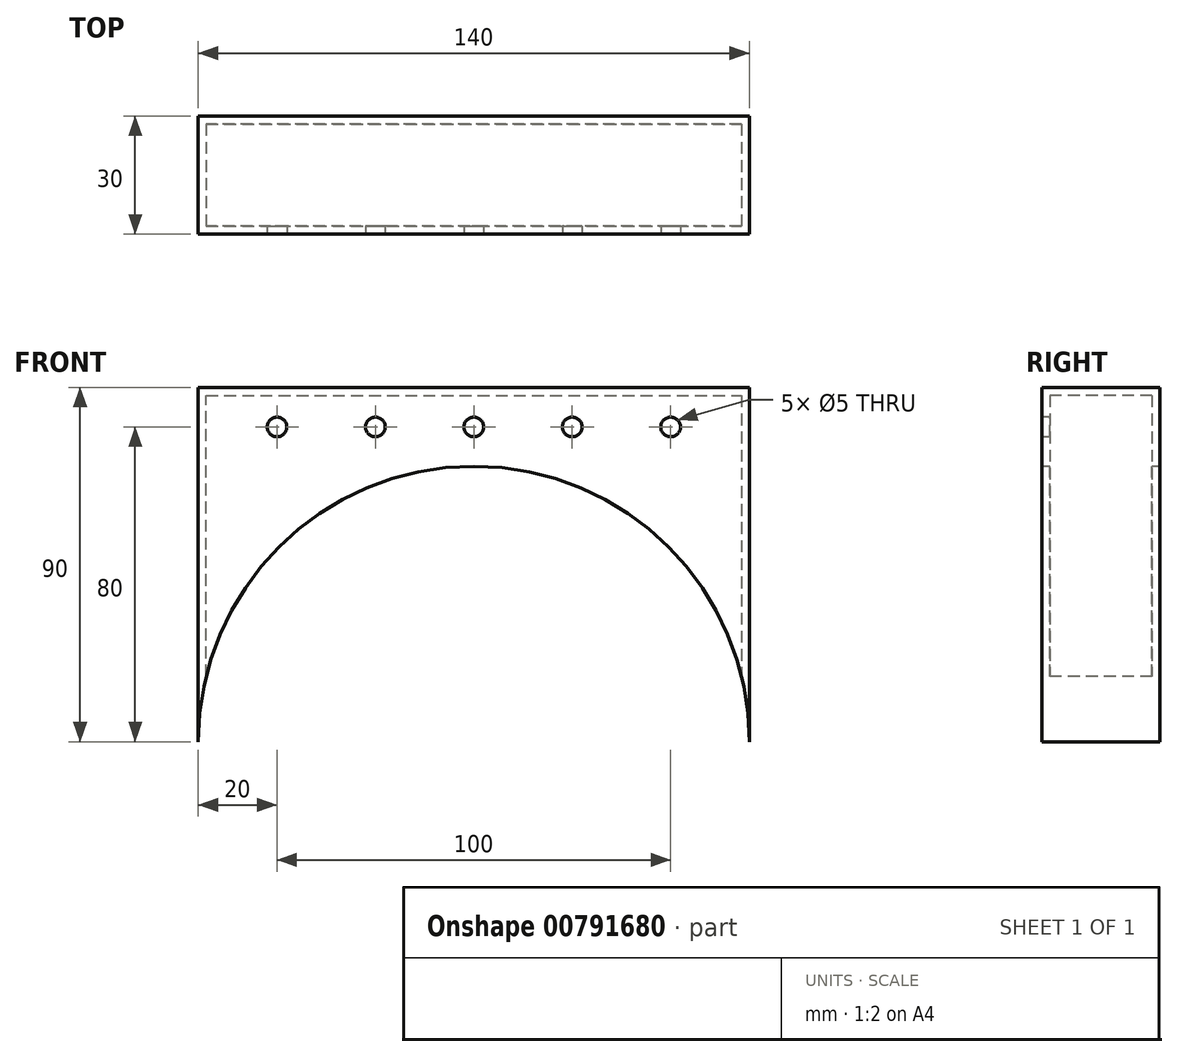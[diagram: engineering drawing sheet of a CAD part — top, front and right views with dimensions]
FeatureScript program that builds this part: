
annotation { "Feature Type Name" : "Feature", "Feature Type Description" : "" }
export const myFeature = defineFeature(function(context is Context, id is Id, definition is map)
    precondition{}
    {
        {
            var Q0;
            Q0=qCreatedBy(makeId("Front.planeOp"),FACE);
            var sketch = newSketch(context, id + "F0", { "sketchPlane" : qUnion([Q0])});
            skArc(sketch, "E0", {"start": v(70, 0) * mm, "mid": v(0, 70) * mm, "end": v(-70, 0) * mm});
            skLineSegment(sketch, "E1", {"start": v(-70, 0.4) * mm, "end": v(-70, 0) * mm});
            skLineSegment(sketch, "E2", {"start": v(-70, 0) * mm, "end": v(-70, 90) * mm});
            skLineSegment(sketch, "E3", {"start": v(-70, 90) * mm, "end": v(70, 90) * mm});
            skLineSegment(sketch, "E4", {"start": v(70, 90) * mm, "end": v(70, 0) * mm});
            skCircle(sketch, "E5", {"center": v(-50, 80) * mm, "radius": 2.5 * mm});
            skCircle(sketch, "E6.1.0.0", {"center": v(-25, 80) * mm, "radius": 2.5 * mm});
            skCircle(sketch, "E6.2.0.0", {"center": v(0, 80) * mm, "radius": 2.5 * mm});
            skCircle(sketch, "E6.3.0.0", {"center": v(25, 80) * mm, "radius": 2.5 * mm});
            skCircle(sketch, "E6.4.0.0", {"center": v(50, 80) * mm, "radius": 2.5 * mm});
            skLineSegment(sketch, "E6.direction1", {"start": v(-50, 80) * mm, "end": v(-25, 80) * mm, "construction": true});
            skPoint(sketch, "E7", {"position": v(0, 70) * mm});
            skSolve(sketch);
        }
        {
            var Q0;
            Q0=makeQuery(id+"F0.imprint","IMPRINT",FACE,{"disambiguationData":[TD([[makeQuery(id+"F0.imprint","IMPRINT",EDGE,{"derivedFrom":sQuery(id+"F0.wireOp",EDGE,"E6.4.0.0")}),1.0]])]});
            var Q1;
            {var subQ2=sQuery(id+"F0.wireOp",EDGE,"E0");Q1=makeQuery(id+"F0.imprint","IMPRINT",FACE,{"disambiguationData":[TD([[makeQuery(id+"F0.imprint","IMPRINT",EDGE,{"derivedFrom":subQ2}),-1.0]])]});}
            var Q2;
            Q2=makeQuery(id+"F0.imprint","IMPRINT",FACE,{"disambiguationData":[TD([[makeQuery(id+"F0.imprint","IMPRINT",EDGE,{"derivedFrom":sQuery(id+"F0.wireOp",EDGE,"E6.3.0.0")}),1.0]])]});
            var Q3;
            Q3=makeQuery(id+"F0.imprint","IMPRINT",FACE,{"disambiguationData":[TD([[makeQuery(id+"F0.imprint","IMPRINT",EDGE,{"derivedFrom":sQuery(id+"F0.wireOp",EDGE,"E6.2.0.0")}),1.0]])]});
            var Q4;
            Q4=makeQuery(id+"F0.imprint","IMPRINT",FACE,{"disambiguationData":[TD([[makeQuery(id+"F0.imprint","IMPRINT",EDGE,{"derivedFrom":sQuery(id+"F0.wireOp",EDGE,"E6.1.0.0")}),1.0]])]});
            var Q5;
            Q5=makeQuery(id+"F0.imprint","IMPRINT",FACE,{"disambiguationData":[TD([[makeQuery(id+"F0.imprint","IMPRINT",EDGE,{"derivedFrom":sQuery(id+"F0.wireOp",EDGE,"E5")}),1.0]])]});
            extrude(context, id + "F1", {"entities" : qUnion([Q0, Q1, Q2, Q3, Q4, Q5]), "oppositeDirection" : true, "depth" : 30 * mm, "offsetDistance" : 25 * mm});
        }
        {
            var Q0;
            Q0=makeQuery(id+"F1.opExtrude","SWEPT_FACE",FACE,{"disambiguationData":[OSD([sQuery(id+"F0.wireOp",EDGE,"E0")])]});
            shell(context, id + "F2", {"entities" : qUnion([Q0]), "thickness" : 2 * mm});
        }
        {
            var Q0;
            Q0=makeQuery(id+"F0.imprint","IMPRINT",FACE,{"disambiguationData":[TD([[makeQuery(id+"F0.imprint","IMPRINT",EDGE,{"derivedFrom":sQuery(id+"F0.wireOp",EDGE,"E6.4.0.0")}),1.0]])]});
            var Q1;
            Q1=makeQuery(id+"F0.imprint","IMPRINT",FACE,{"disambiguationData":[TD([[makeQuery(id+"F0.imprint","IMPRINT",EDGE,{"derivedFrom":sQuery(id+"F0.wireOp",EDGE,"E6.3.0.0")}),1.0]])]});
            var Q2;
            Q2=makeQuery(id+"F0.imprint","IMPRINT",FACE,{"disambiguationData":[TD([[makeQuery(id+"F0.imprint","IMPRINT",EDGE,{"derivedFrom":sQuery(id+"F0.wireOp",EDGE,"E6.2.0.0")}),1.0]])]});
            var Q3;
            Q3=makeQuery(id+"F0.imprint","IMPRINT",FACE,{"disambiguationData":[TD([[makeQuery(id+"F0.imprint","IMPRINT",EDGE,{"derivedFrom":sQuery(id+"F0.wireOp",EDGE,"E6.1.0.0")}),1.0]])]});
            var Q4;
            Q4=makeQuery(id+"F0.imprint","IMPRINT",FACE,{"disambiguationData":[TD([[makeQuery(id+"F0.imprint","IMPRINT",EDGE,{"derivedFrom":sQuery(id+"F0.wireOp",EDGE,"E5")}),1.0]])]});
            var Q5;
            Q5=sQuery(id+"F0.wireOp",EDGE,"E6.4.0.0");
            var Q6;
            Q6=sQuery(id+"F0.wireOp",EDGE,"E6.3.0.0");
            var Q7;
            Q7=sQuery(id+"F0.wireOp",EDGE,"E6.2.0.0");
            var Q8;
            Q8=sQuery(id+"F0.wireOp",EDGE,"E6.1.0.0");
            var Q9;
            Q9=sQuery(id+"F0.wireOp",EDGE,"E5");
            extrude(context, id + "F3", {"entities" : qUnion([Q0, Q1, Q2, Q3, Q4]), "operationType" : NewBodyOperationType.REMOVE, "surfaceEntities" : qUnion([Q5, Q6, Q7, Q8, Q9]), "oppositeDirection" : true, "depth" : 5 * mm, "offsetDistance" : 25 * mm});
        }
    });
